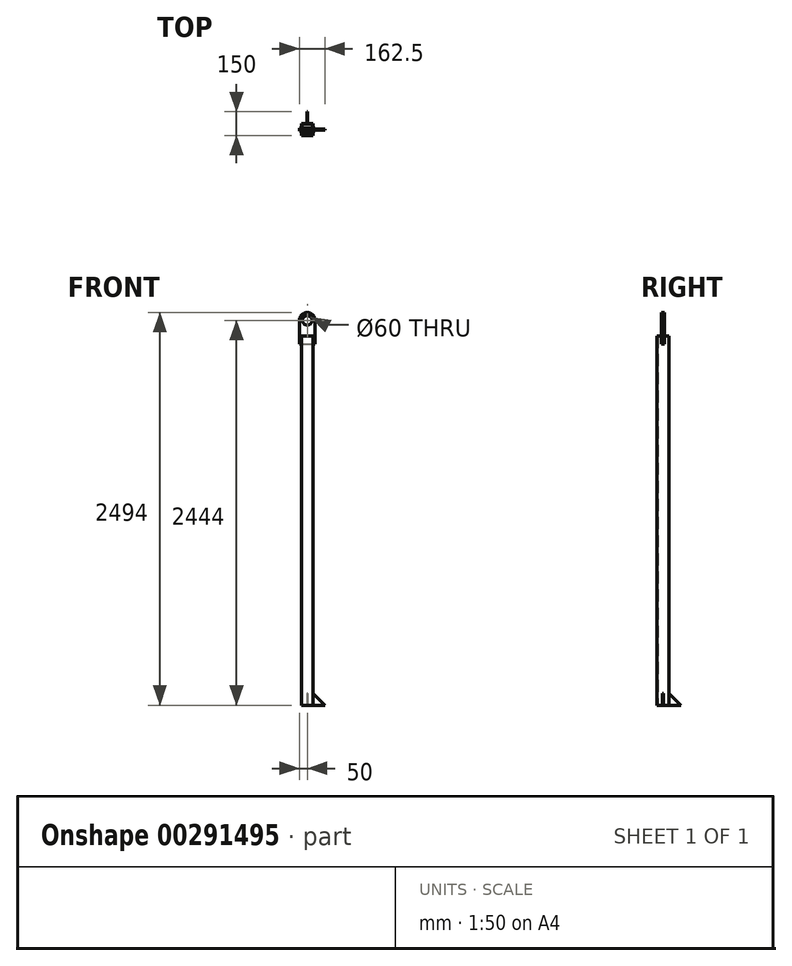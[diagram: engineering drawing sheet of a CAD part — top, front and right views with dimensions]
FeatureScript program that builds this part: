
annotation { "Feature Type Name" : "Feature", "Feature Type Description" : "" }
export const myFeature = defineFeature(function(context is Context, id is Id, definition is map)
    precondition{}
    {
        {
            var Q0;
            Q0=qCreatedBy(makeId("Top.planeOp"),FACE);
            var sketch = newSketch(context, id + "F0", { "sketchPlane" : qUnion([Q0])});
            skLineSegment(sketch, "E0.bottom", {"start": v(37.5, 37.5) * mm, "end": v(-37.5, 37.5) * mm});
            skLineSegment(sketch, "E0.top", {"start": v(37.5, -37.5) * mm, "end": v(-37.5, -37.5) * mm});
            skLineSegment(sketch, "E0.left", {"start": v(37.5, 37.5) * mm, "end": v(37.5, -37.5) * mm});
            skLineSegment(sketch, "E0.right", {"start": v(-37.5, 37.5) * mm, "end": v(-37.5, -37.5) * mm});
            skPoint(sketch, "E0.middle", {"position": v(0, 0) * mm});
            skLineSegment(sketch, "E1.0", {"start": v(33, 33) * mm, "end": v(-33, 33) * mm});
            skLineSegment(sketch, "E2.0", {"start": v(-33, 33) * mm, "end": v(-33, -33) * mm});
            skLineSegment(sketch, "E3.0", {"start": v(33, -33) * mm, "end": v(-33, -33) * mm});
            skLineSegment(sketch, "E4.0", {"start": v(33, 33) * mm, "end": v(33, -33) * mm});
            skSolve(sketch);
        }
        {
            var Q0;
            Q0=qSketchRegion(id+"F0",true);
            extrude(context, id + "F1", {"entities" : qUnion([Q0]), "depth" : 2344 * mm});
        }
        {
            var Q0;
            Q0=qCreatedBy(makeId("Front.planeOp"),FACE);
            var sketch = newSketch(context, id + "F2", { "sketchPlane" : qUnion([Q0])});
            skLineSegment(sketch, "E5.bottom", {"start": v(-50, 2294) * mm, "end": v(50, 2294) * mm});
            skLineSegment(sketch, "E5.left", {"start": v(-50, 2294) * mm, "end": v(-50, 2444) * mm});
            skLineSegment(sketch, "E5.right", {"start": v(50, 2294) * mm, "end": v(50, 2444) * mm});
            skPoint(sketch, "E6.firstSnap0", {"position": v(0, 2294) * mm});
            skCircle(sketch, "E7", {"center": v(0, 2444) * mm, "radius": 30 * mm});
            skArc(sketch, "E8", {"start": v(50, 2444) * mm, "mid": v(0, 2494) * mm, "end": v(-50, 2444) * mm});
            skSolve(sketch);
        }
        {
            var Q0;
            Q0=qSketchRegion(id+"F2",true);
            extrude(context, id + "F3", {"entities" : qUnion([Q0]), "operationType" : NewBodyOperationType.ADD, "endBound" : BoundingType.SYMMETRIC, "depth" : 19 * mm});
        }
        {
            var Q0;
            Q0=qCreatedBy(makeId("Front.planeOp"),FACE);
            var sketch = newSketch(context, id + "F4", { "sketchPlane" : qUnion([Q0])});
            skLineSegment(sketch, "E9", {"start": v(37.5, 0) * mm, "end": v(112.5, 0) * mm});
            skLineSegment(sketch, "E10", {"start": v(112.5, 0) * mm, "end": v(37.5, 75) * mm});
            skLineSegment(sketch, "E11", {"start": v(37.5, 75) * mm, "end": v(37.5, 0) * mm});
            skSolve(sketch);
        }
        {
            var Q0;
            Q0 = qSketchRegion(id + "F4", true);
            extrude(context, id + "F5", {"entities" : qUnion([Q0]), "operationType" : NewBodyOperationType.ADD, "endBound" : BoundingType.SYMMETRIC, "depth" : 6 * mm});
        }
        {
            var Q0;
            Q0=qCreatedBy(makeId("Right.planeOp"),FACE);
            var sketch = newSketch(context, id + "F6", { "sketchPlane" : qUnion([Q0])});
            skLineSegment(sketch, "E12", {"start": v(37.5, 0) * mm, "end": v(112.5, 0) * mm});
            skLineSegment(sketch, "E13", {"start": v(112.5, 0) * mm, "end": v(37.5, 75) * mm});
            skLineSegment(sketch, "E14", {"start": v(37.5, 75) * mm, "end": v(37.5, 0) * mm});
            skSolve(sketch);
        }
        {
            var Q0;
            Q0 = qSketchRegion(id + "F6", true);
            extrude(context, id + "F7", {"entities" : qUnion([Q0]), "operationType" : NewBodyOperationType.ADD, "endBound" : BoundingType.SYMMETRIC, "depth" : 6 * mm});
        }
    });
